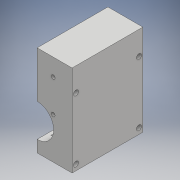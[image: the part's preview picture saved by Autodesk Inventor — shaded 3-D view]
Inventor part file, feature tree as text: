
AUTODESK INVENTOR PART (.ipt)
format: ipt  version: 2018 (Build 220112000, 112)  size: 412,160 bytes
history: native  units: mm
features: sketch x21, projected_geometry x20, extrude x17, hole x4, fillet x3, chamfer x1
ambient origin geometry x8: Origin, YZ Plane, XZ Plane, XY Plane, X Axis, Y Axis, Z Axis, Center Point
bodies: Solid1 (feature_tree)
feature tree (66):
  extrude  "Extrusion1"  Depth=45.0mm
  extrude  "Extrusion2"  Depth=1.95mm
  hole  "Hole1"  [1 undecoded]
  hole  "Hole2"  [1 undecoded]
  fillet  "Fillet1"  Radius=14.0mm
  extrude  "Extrusion3"  Depth=18.5mm
  extrude  "Extrusion4"  Depth=10.0mm
  extrude  "Extrusion5"  Depth=2.195mm
  extrude  "Extrusion6"  Depth=20.5mm
  hole  "Hole3"  [1 undecoded]
  extrude  "Extrusion7"  Depth=0.5mm
  extrude  "Extrusion8"  Depth=5.0mm TaperAngle=0.0deg
  extrude  "Extrusion9"  Depth=10.0mm
  extrude  "Extrusion10"  Depth=10.0mm
  extrude  "Extrusion11"  Depth=14.5mm
  extrude  "Extrusion12"  Depth=14.5mm
  extrude  "Extrusion13"  Depth=5.0mm
  extrude  "Extrusion14"  Depth=5.0mm
  extrude  "Extrusion15"  Depth=5.0mm
  extrude  "Extrusion16"  Depth=9.0mm
  extrude  "Extrusion17"  Depth=14.75mm
  chamfer  "Chamfer1"  Distance=4.0mm
  fillet  "Fillet7"  Radius=1.0mm
  hole  "Hole4"  [1 undecoded]
  fillet  "Fillet8"  Radius=32.0mm
  sketch  "Sketch1"  dims[d0=24.5mm d1=45.0mm]
  sketch  "Sketch2"  dims[d2=1.95mm d3=0.0mm d4=2.25mm]
  projected_geometry  "Projected Loop1"
  sketch  "Sketch3"  dims[d5=20.0mm d6=2.25mm]
  projected_geometry  "Projected Loop2"
  sketch  "Sketch4"  dims[d7=5.25mm d8=5.25mm d9=14.0mm]
  projected_geometry  "Projected Loop3"
  sketch  "Sketch5"  dims[d10=5.25mm d11=18.5mm]
  projected_geometry  "Projected Loop4"
  sketch  "Sketch6"  dims[d12=10.0mm d13=0.0mm d14=20.5mm]
  projected_geometry  "Projected Loop5"
  sketch  "Sketch7"  dims[d15=2.0mm d16=2.195mm]
  projected_geometry  "Projected Loop6"
  sketch  "Sketch8"  dims[d17=2.0mm]
  projected_geometry  "Projected Loop7"
  sketch  "Sketch9"  dims[d18=2.4mm d19=6.0mm d20=4.4mm d21=2.0mm d22=90.0deg d23=8.0mm d24=20.594885mm d25=20.5mm]
  projected_geometry  "Projected Loop8"
  projected_geometry  "Projected Loop9"
  sketch  "Sketch10"  dims[d26=26.65mm d27=2.0mm]
  projected_geometry  "Projected Loop10"
  projected_geometry  "Projected Loop11"
  sketch  "Sketch11"  dims[d28=2.0mm]
  projected_geometry  "Projected Loop12"
  sketch  "Sketch12"  dims[d29=2.4mm d30=6.0mm d31=4.4mm d32=2.0mm d33=90.0deg d34=8.0mm d35=20.594885mm d36=0.5mm]
  sketch  "Sketch13"  dims[d37=18.0mm d38=5.0mm d39=0.0mm]
  sketch  "Sketch14"  dims[d41=10.0mm d42=0.0mm d43=24.5mm]
  projected_geometry  "Projected Loop13"
  sketch  "Sketch15"  dims[d44=1.15mm d45=0.0mm d46=10.0mm]
  sketch  "Sketch16"  dims[d47=21.0mm d48=14.5mm]
  projected_geometry  "Projected Loop14"
  sketch  "Sketch17"  dims[d49=20.0mm d50=14.5mm]
  projected_geometry  "Projected Loop15"
  sketch  "Sketch18"  dims[d51=24.5mm d52=5.0mm]
  projected_geometry  "Projected Loop16"
  sketch  "Sketch19"  dims[d53=5.0mm d54=2.25mm]
  projected_geometry  "Projected Loop17"
  sketch  "Sketch20"  dims[d55=2.25mm d56=5.0mm]
  projected_geometry  "Projected Loop18"
  sketch  "Sketch21"  dims[d57=5.0mm d58=9.0mm d59=14.75mm d60=4.0mm d61=1.0mm d62=0.0mm d63=20.7mm d64=2.4mm d65=6.0mm d66=4.4mm d67=2.0mm d68=90.0deg d69=8.0mm d70=20.594885mm d72=32.0mm d73=5.0mm d74=0.0mm d75=1.0mm d76=0.0mm d77=12.25mm d78=0.0mm d80=8.0mm d81=4.5mm d82=0.0mm d84=0.2mm d85=0.0mm d86=21.0mm d87=0.5mm d88=0.0mm d91=8.0mm d92=0.0mm d93=5.0mm d94=0.0mm d95=5.0mm d96=0.0mm d98=0.2mm d99=0.0mm d100=0.2mm d101=0.0mm d102=2.5mm d103=2.0mm d104=45.0deg d105=1.5mm d106=8.0mm d107=3.2mm d108=5.029mm d109=6.3mm d110=2.0mm d111=90.0deg d112=7.675mm d113=20.594885mm d114=0.5mm]
  projected_geometry  "Projected Loop19"
  projected_geometry  "Projected Loop20"
note: 4 required parameter values undecoded (feature->parameter linkage not recoverable at this tier; creation-order binding heuristic only, values carry confidence <= 0.55)
